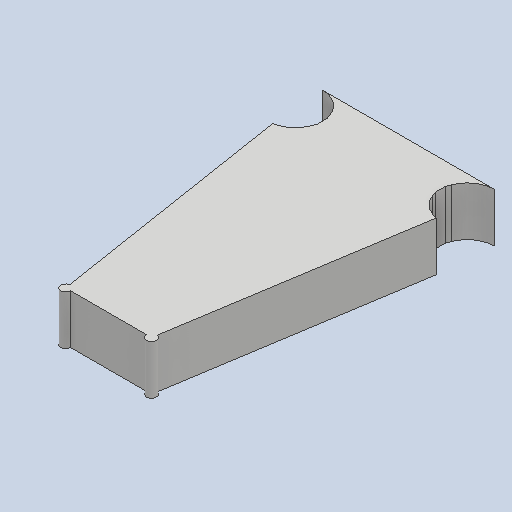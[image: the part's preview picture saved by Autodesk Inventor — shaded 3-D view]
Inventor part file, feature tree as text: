
AUTODESK INVENTOR PART (.ipt)
format: ipt  version: 2025 (Build 290162010, 162A)  size: 122,368 bytes
history: native  units: mm
features: other x1, extrude x1, sketch x1
ambient origin geometry x8: Origin, YZ Plane, XZ Plane, XY Plane, X Axis, Y Axis, Z Axis, Center Point
bodies: Body1 (feature_tree)
feature tree (3):
  other  "Твердое тело1"
  extrude  "Выдавливание1"  Depth=90.0mm
  sketch  "Эскиз1"
